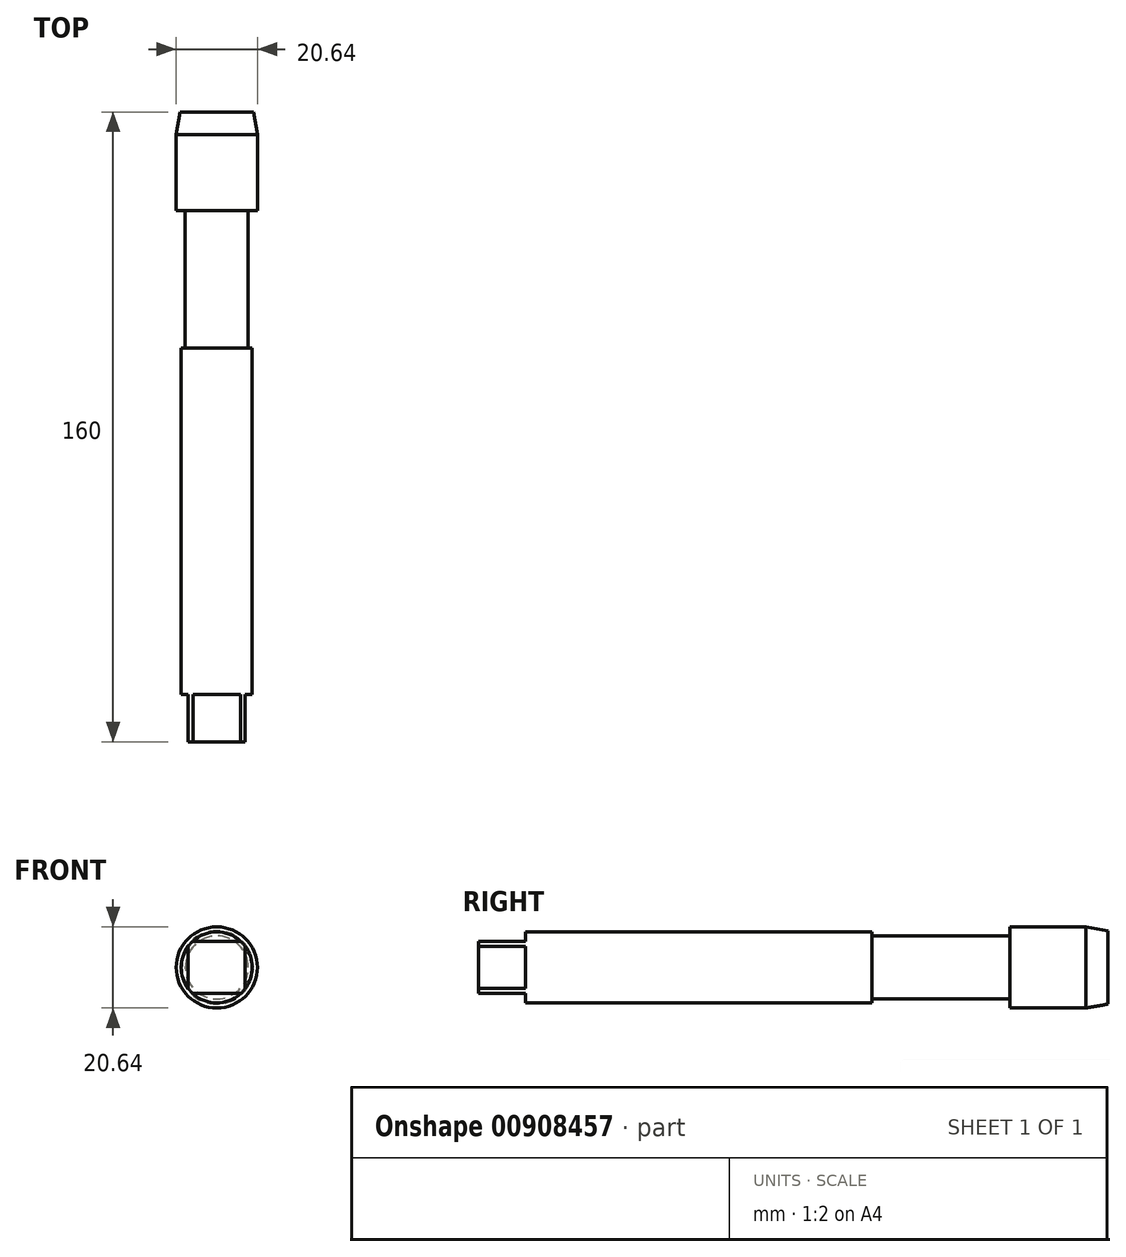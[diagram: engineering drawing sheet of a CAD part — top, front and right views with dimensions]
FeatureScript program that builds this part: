
annotation { "Feature Type Name" : "Feature", "Feature Type Description" : "" }
export const myFeature = defineFeature(function(context is Context, id is Id, definition is map)
    precondition{}
    {
        {
            var Q0;
            Q0=qCreatedBy(makeId("Front.planeOp"),FACE);
            var sketch = newSketch(context, id + "F0", { "sketchPlane" : qUnion([Q0])});
            skCircle(sketch, "E0", {"center": v(0, 0) * mm, "radius": 9 * mm});
            skSolve(sketch);
        }
        {
            var Q0;
            Q0=makeQuery(id+"F0.imprint","IMPRINT",FACE,{"disambiguationData":[TD([[makeQuery(id+"F0.imprint","IMPRINT",EDGE,{"derivedFrom":sQuery(id+"F0.wireOp",EDGE,"E0")}),1.0]])]});
            extrude(context, id + "F1", {"entities" : qUnion([Q0]), "depth" : 160 * mm, "offsetDistance" : 25 * mm});
        }
        {
            var Q0;
            Q0=makeQuery(id+"F1.opExtrude","CAP_FACE",FACE,{"disambiguationData":[OSD([sQuery(id+"F0.wireOp",EDGE,"E0")])],"isStart":false});
            var sketch = newSketch(context, id + "F2", { "sketchPlane" : qUnion([Q0])});
            skLineSegment(sketch, "E1.bottom", {"start": v(-7.25, -6.64) * mm, "end": v(7.25, -6.64) * mm});
            skLineSegment(sketch, "E1.top", {"start": v(-7.25, 6.64) * mm, "end": v(7.25, 6.64) * mm});
            skLineSegment(sketch, "E1.left", {"start": v(-7.25, -6.64) * mm, "end": v(-7.25, 6.64) * mm});
            skLineSegment(sketch, "E1.right", {"start": v(7.25, -6.64) * mm, "end": v(7.25, 6.64) * mm});
            skPoint(sketch, "E1.middle", {"position": v(0, 0) * mm});
            skLineSegment(sketch, "E2.bottom", {"start": v(-11.7, -11.32) * mm, "end": v(11.7, -11.32) * mm});
            skLineSegment(sketch, "E2.top", {"start": v(-11.7, 11.32) * mm, "end": v(11.7, 11.32) * mm});
            skLineSegment(sketch, "E2.left", {"start": v(-11.7, -11.32) * mm, "end": v(-11.7, 11.32) * mm});
            skLineSegment(sketch, "E2.right", {"start": v(11.7, -11.32) * mm, "end": v(11.7, 11.32) * mm});
            skSolve(sketch);
        }
        {
            var Q0;
            Q0 = qSketchRegion(id + "F2", true);
            extrude(context, id + "F3", {"entities" : qUnion([Q0]), "operationType" : NewBodyOperationType.REMOVE, "oppositeDirection" : true, "depth" : 12 * mm, "offsetDistance" : 25 * mm});
        }
        {
            var Q0;
            Q0=makeQuery(id+"F1.opExtrude","CAP_FACE",FACE,{"disambiguationData":[OSD([sQuery(id+"F0.wireOp",EDGE,"E0")])],"isStart":true});
            var sketch = newSketch(context, id + "F4", { "sketchPlane" : qUnion([Q0])});
            skCircle(sketch, "E3", {"center": v(0, 0) * mm, "radius": 10.31 * mm});
            skSolve(sketch);
        }
        {
            var Q0;
            Q0 = qSketchRegion(id + "F4", true);
            extrude(context, id + "F5", {"entities" : qUnion([Q0]), "operationType" : NewBodyOperationType.ADD, "oppositeDirection" : true, "depth" : 25 * mm, "offsetDistance" : 25 * mm});
        }
        {
            var Q0;
            Q0=makeQuery(id+"F5.opExtrude","CAP_EDGE",EDGE,{"disambiguationData":[OSD([sQuery(id+"F4.wireOp",EDGE,"E3")])],"isStart":true});
            chamfer(context, id + "F6", {"entities" : qUnion([Q0]), "chamferType" : ChamferType.OFFSET_ANGLE, "width" : 1 * mm, "oppositeDirection" : false, "angle" : 80 * degree, "tangentPropagation" : true});
        }
        {
            var Q0;
            Q0=makeQuery(id+"F5.opExtrude","CAP_FACE",FACE,{"disambiguationData":[OSD([sQuery(id+"F4.wireOp",EDGE,"E3")])],"isStart":false});
            var sketch = newSketch(context, id + "F7", { "sketchPlane" : qUnion([Q0])});
            skCircle(sketch, "E4", {"center": v(0, 0) * mm, "radius": 8 * mm});
            skCircle(sketch, "E5", {"center": v(0, 0) * mm, "radius": 14.76 * mm});
            skSolve(sketch);
        }
        {
            var Q0;
            Q0 = qSketchRegion(id + "F7", true);
            extrude(context, id + "F8", {"entities" : qUnion([Q0]), "operationType" : NewBodyOperationType.REMOVE, "depth" : 35 * mm, "offsetDistance" : 25 * mm});
        }
    });
